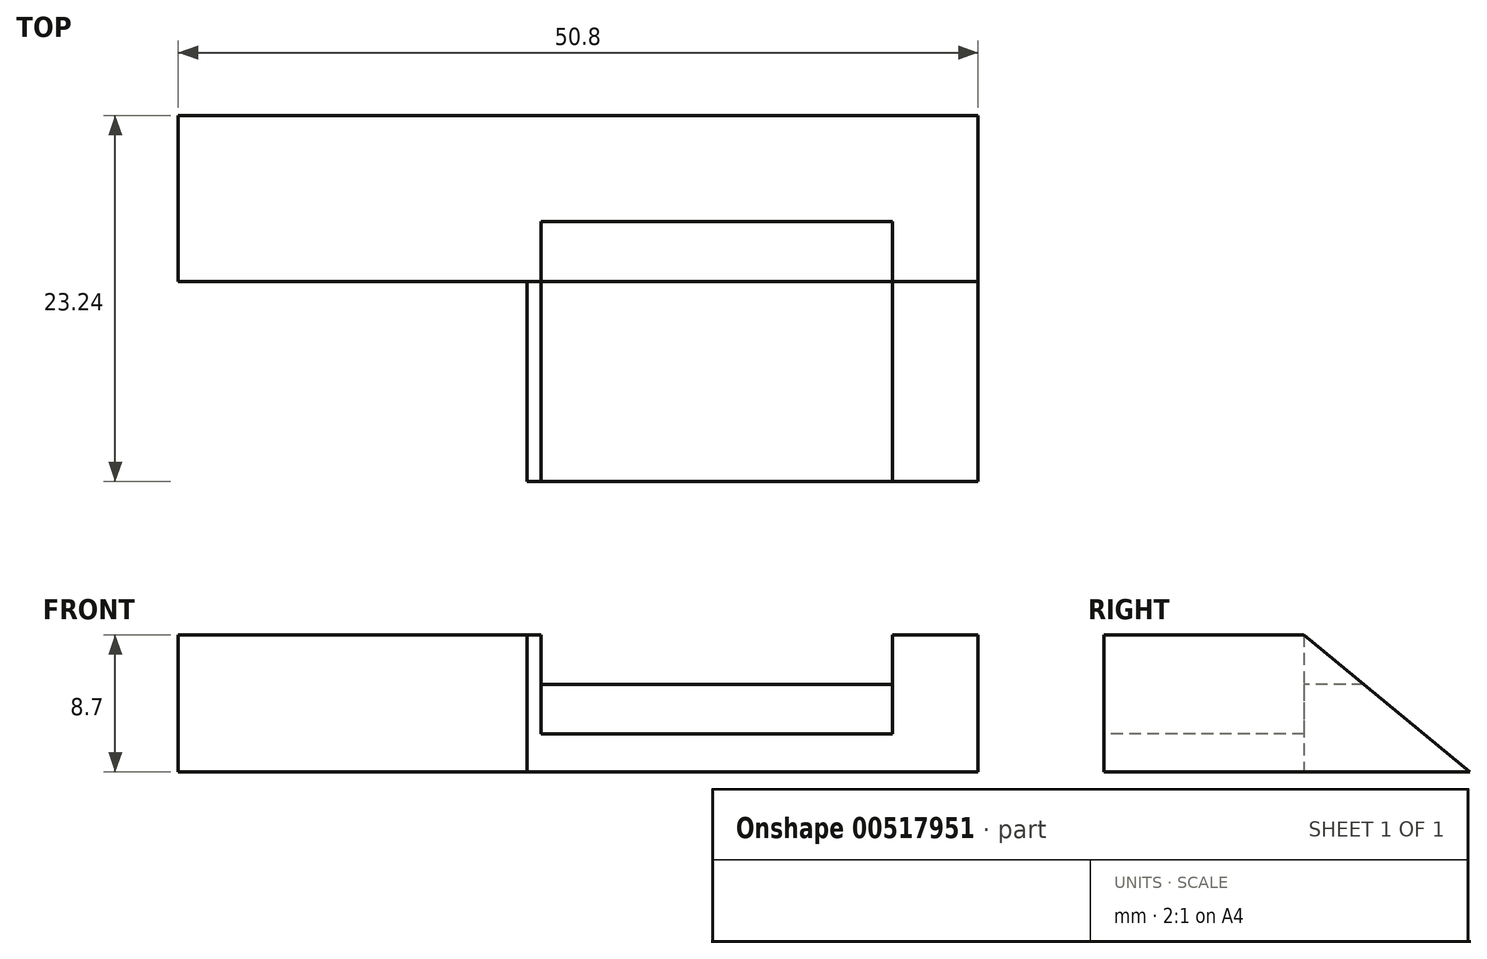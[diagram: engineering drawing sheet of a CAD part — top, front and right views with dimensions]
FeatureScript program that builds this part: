
annotation { "Feature Type Name" : "Feature", "Feature Type Description" : "" }
export const myFeature = defineFeature(function(context is Context, id is Id, definition is map)
    precondition{}
    {
        {
            var Q0;
            Q0=qCreatedBy(makeId("Front.planeOp"),FACE);
            var sketch = newSketch(context, id + "F0", { "sketchPlane" : qUnion([Q0])});
            skLineSegment(sketch, "E0.bottom", {"start": v(14.33, 4.35) * mm, "end": v(-14.33, 4.35) * mm});
            skLineSegment(sketch, "E0.top", {"start": v(14.33, -4.35) * mm, "end": v(-14.33, -4.35) * mm});
            skLineSegment(sketch, "E0.left", {"start": v(14.33, 4.35) * mm, "end": v(14.33, -4.35) * mm});
            skLineSegment(sketch, "E0.right", {"start": v(-14.33, 4.35) * mm, "end": v(-14.33, -4.35) * mm});
            skPoint(sketch, "E0.middle", {"position": v(0, 0) * mm});
            skSolve(sketch);
        }
        {
            var Q0;
            Q0 = qSketchRegion(id + "F0", true);
            extrude(context, id + "F1", {"entities" : qUnion([Q0]), "depth" : -12.7 * mm, "offsetDistance" : 25.4 * mm});
        }
        {
            var Q0;
            Q0=makeQuery(id+"F1.opExtrude","CAP_FACE",FACE,{"disambiguationData":[OSD([sQuery(id+"F0.wireOp",EDGE,"E0.bottom"),sQuery(id+"F0.wireOp",EDGE,"E0.top"),sQuery(id+"F0.wireOp",EDGE,"E0.left"),sQuery(id+"F0.wireOp",EDGE,"E0.right")])],"isStart":true});
            var sketch = newSketch(context, id + "F2", { "sketchPlane" : qUnion([Q0])});
            skLineSegment(sketch, "E1.bottom", {"start": v(-13.42, 4.35) * mm, "end": v(8.88, 4.35) * mm});
            skLineSegment(sketch, "E1.top", {"start": v(-13.42, -1.92) * mm, "end": v(8.88, -1.92) * mm});
            skLineSegment(sketch, "E1.left", {"start": v(-13.42, 4.35) * mm, "end": v(-13.42, -1.92) * mm});
            skLineSegment(sketch, "E1.right", {"start": v(8.88, 4.35) * mm, "end": v(8.88, -1.92) * mm});
            skSolve(sketch);
        }
        {
            var Q0;
            Q0 = qSketchRegion(id + "F2", true);
            extrude(context, id + "F3", {"entities" : qUnion([Q0]), "operationType" : NewBodyOperationType.REMOVE, "oppositeDirection" : true, "depth" : 50.8 * mm, "offsetDistance" : 25.4 * mm});
        }
        {
            var Q0;
            Q0=makeQuery(id+"F1.opExtrude","SWEPT_FACE",FACE,{"disambiguationData":[OSD([sQuery(id+"F0.wireOp",EDGE,"E0.left")])]});
            var sketch = newSketch(context, id + "F4", { "sketchPlane" : qUnion([Q0])});
            skLineSegment(sketch, "E2", {"start": v(12.7, -4.35) * mm, "end": v(23.24, -4.35) * mm});
            skLineSegment(sketch, "E3", {"start": v(23.24, -4.35) * mm, "end": v(12.7, 4.35) * mm});
            skLineSegment(sketch, "E4", {"start": v(12.7, 4.35) * mm, "end": v(12.7, -4.35) * mm});
            skSolve(sketch);
        }
        {
            var Q0;
            Q0 = qSketchRegion(id + "F4", true);
            extrude(context, id + "F5", {"entities" : qUnion([Q0]), "operationType" : NewBodyOperationType.ADD, "depth" : -50.8 * mm, "offsetDistance" : 25.4 * mm});
        }
        {
            var Q0;
            Q0=makeQuery(id+"F5.boolean.opBoolean","SPLIT",FACE,{"disambiguationData":[TD([makeQuery(id+"F3.boolean.opBoolean","COPY",FACE,{"derivedFrom":makeQuery(id+"F3.opExtrude","SWEPT_FACE",FACE,{"disambiguationData":[OSD([sQuery(id+"F2.wireOp",EDGE,"E1.top")])]})})])],"derivedFrom":makeQuery(id+"F5.opExtrude","SWEPT_FACE",FACE,{"disambiguationData":[OSD([sQuery(id+"F4.wireOp",EDGE,"E4")])]})});
            var sketch = newSketch(context, id + "F6", { "sketchPlane" : qUnion([Q0])});
            skLineSegment(sketch, "E5.bottom", {"start": v(-13.42, 4.35) * mm, "end": v(8.88, 4.35) * mm});
            skLineSegment(sketch, "E5.top", {"start": v(-13.42, 1.21) * mm, "end": v(8.88, 1.21) * mm});
            skLineSegment(sketch, "E5.left", {"start": v(-13.42, 4.35) * mm, "end": v(-13.42, 1.21) * mm});
            skLineSegment(sketch, "E5.right", {"start": v(8.88, 4.35) * mm, "end": v(8.88, 1.21) * mm});
            skSolve(sketch);
        }
        {
            var Q0;
            Q0 = qSketchRegion(id + "F6", true);
            extrude(context, id + "F7", {"entities" : qUnion([Q0]), "operationType" : NewBodyOperationType.REMOVE, "oppositeDirection" : true, "depth" : 25.4 * mm, "offsetDistance" : 25.4 * mm});
        }
    });
